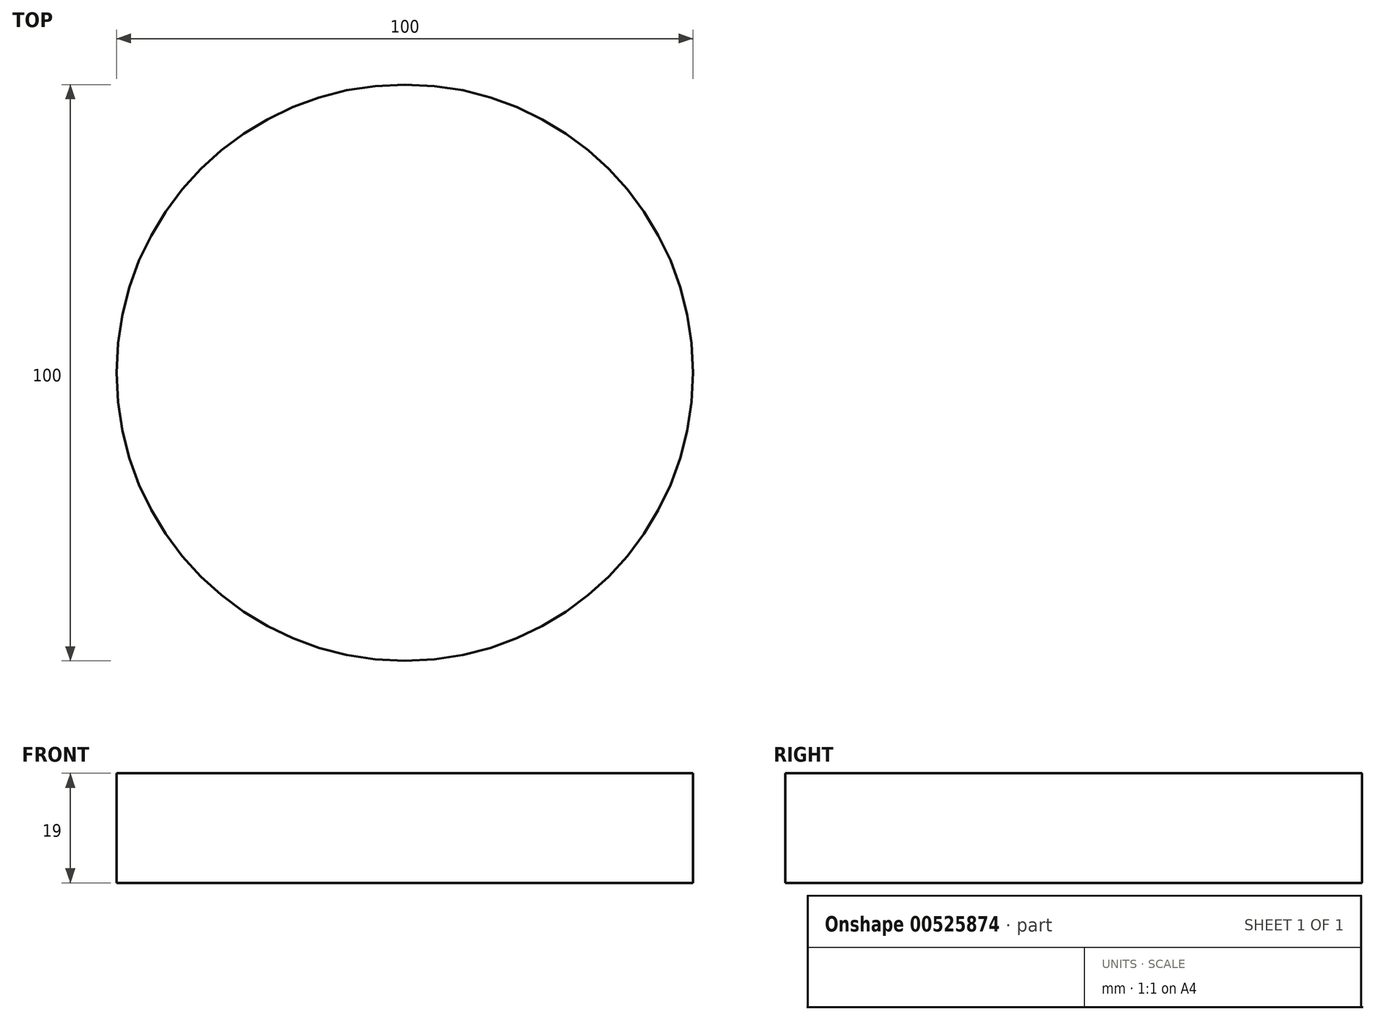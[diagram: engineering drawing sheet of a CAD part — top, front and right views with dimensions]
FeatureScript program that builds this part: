
annotation { "Feature Type Name" : "Feature", "Feature Type Description" : "" }
export const myFeature = defineFeature(function(context is Context, id is Id, definition is map)
    precondition{}
    {
        {
            var Q0;
            Q0=qCreatedBy(makeId("Top.planeOp"),FACE);
            var sketch = newSketch(context, id + "F0", { "sketchPlane" : qUnion([Q0])});
            skCircle(sketch, "E0", {"center": v(0, 0) * mm, "radius": 50 * mm});
            skSolve(sketch);
        }
        {
            var Q0;
            Q0 = qSketchRegion(id + "F0", true);
            extrude(context, id + "F1", {"entities" : qUnion([Q0]), "depth" : 19 * mm, "offsetDistance" : 25 * mm});
        }
    });
